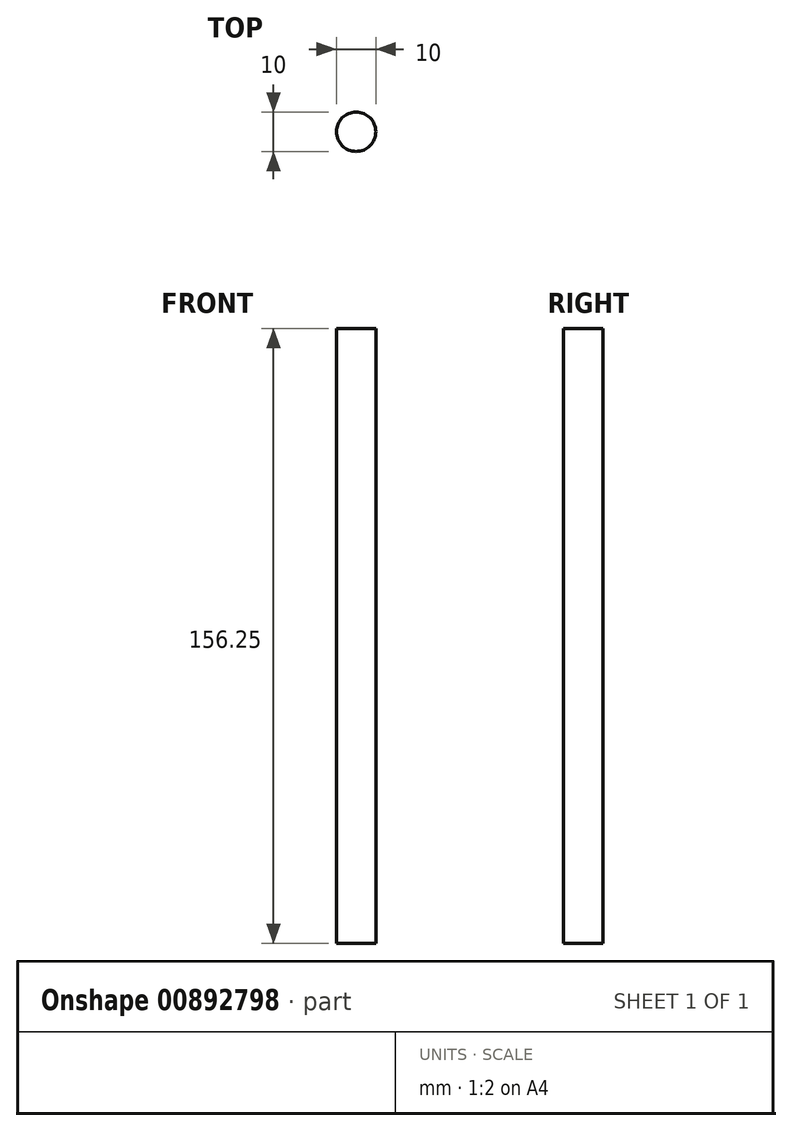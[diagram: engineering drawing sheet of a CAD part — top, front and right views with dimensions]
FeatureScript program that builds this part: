
annotation { "Feature Type Name" : "Feature", "Feature Type Description" : "" }
export const myFeature = defineFeature(function(context is Context, id is Id, definition is map)
    precondition{}
    {
        {
            var Q0;
            Q0=qCreatedBy(makeId("Top.planeOp"),FACE);
            var sketch = newSketch(context, id + "F0", { "sketchPlane" : qUnion([Q0])});
            skCircle(sketch, "E0", {"center": v(0, 0) * mm, "radius": 5 * mm});
            skSolve(sketch);
        }
        {
            var Q0;
            Q0=makeQuery(id+"F0.imprint","IMPRINT",FACE,{"disambiguationData":[TD([[makeQuery(id+"F0.imprint","IMPRINT",EDGE,{"derivedFrom":sQuery(id+"F0.wireOp",EDGE,"E0")}),1.0]])]});
            extrude(context, id + "F1", {"entities" : qUnion([Q0]), "depth" : 156.25 * mm, "offsetDistance" : 25 * mm});
        }
    });
